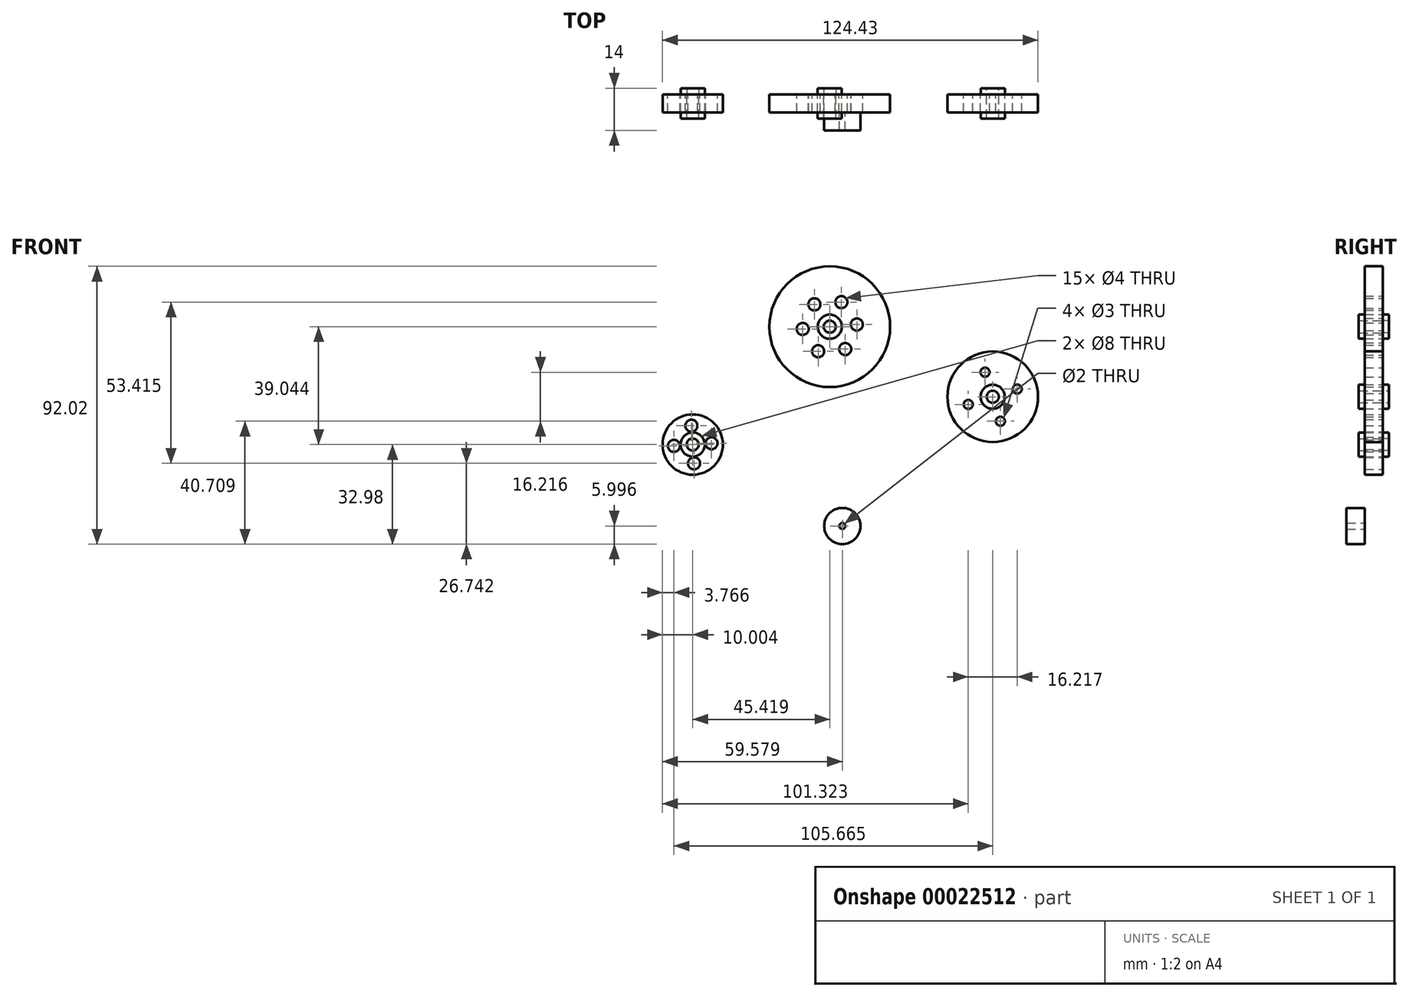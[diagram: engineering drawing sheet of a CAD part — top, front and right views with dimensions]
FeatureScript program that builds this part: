
annotation { "Feature Type Name" : "Feature", "Feature Type Description" : "" }
export const myFeature = defineFeature(function(context is Context, id is Id, definition is map)
    precondition{}
    {
        {
            var Q0;
            Q0=qCreatedBy(makeId("Front.planeOp"),FACE);
            var sketch = newSketch(context, id + "F0", { "sketchPlane" : qUnion([Q0])});
            skCircle(sketch, "E0", {"center": v(-11.19, 16.31) * mm, "radius": 20 * mm});
            skCircle(sketch, "E1", {"center": v(-11.19, 16.31) * mm, "radius": 4 * mm});
            skCircle(sketch, "E2", {"center": v(-11.19, 16.31) * mm, "radius": 2 * mm});
            skCircle(sketch, "E3", {"center": v(-6.07, 8.91) * mm, "radius": 2 * mm});
            skCircle(sketch, "E4.1.0", {"center": v(-2.22, 17.04) * mm, "radius": 2 * mm});
            skCircle(sketch, "E4.2.0", {"center": v(-7.33, 24.45) * mm, "radius": 2 * mm});
            skCircle(sketch, "E4.3.0", {"center": v(-16.3, 23.72) * mm, "radius": 2 * mm});
            skCircle(sketch, "E4.4.0", {"center": v(-20.16, 15.58) * mm, "radius": 2 * mm});
            skCircle(sketch, "E4.5.0", {"center": v(-15.04, 8.18) * mm, "radius": 2 * mm});
            skSolve(sketch);
        }
        {
            var Q0;
            Q0=makeQuery(id+"F0.imprint","IMPRINT",FACE,{"disambiguationData":[TD([[makeQuery(id+"F0.imprint","IMPRINT",EDGE,{"derivedFrom":sQuery(id+"F0.wireOp",EDGE,"E0")}),1.0]])]});
            extrude(context, id + "F1", {"entities" : qUnion([Q0]), "depth" : 6 * mm});
        }
        {
            var Q0;
            Q0=makeQuery(id+"F0.imprint","IMPRINT",FACE,{"disambiguationData":[TD([[makeQuery(id+"F0.imprint","IMPRINT",EDGE,{"derivedFrom":sQuery(id+"F0.wireOp",EDGE,"E1")}),1.0]])]});
            extrude(context, id + "F2", {"entities" : qUnion([Q0]), "operationType" : NewBodyOperationType.ADD, "oppositeDirection" : true, "depth" : 2 * mm});
        }
        {
            var Q0;
            Q0=makeQuery(id+"F0.imprint","IMPRINT",FACE,{"disambiguationData":[TD([[makeQuery(id+"F0.imprint","IMPRINT",EDGE,{"derivedFrom":sQuery(id+"F0.wireOp",EDGE,"E1")}),1.0]])]});
            extrude(context, id + "F3", {"entities" : qUnion([Q0]), "depth" : 8 * mm});
        }
        {
            var Q0;
            Q0=qCreatedBy(makeId("Front.planeOp"),FACE);
            var sketch = newSketch(context, id + "F4", { "sketchPlane" : qUnion([Q0])});
            skCircle(sketch, "E5", {"center": v(42.82, -6.9) * mm, "radius": 15 * mm});
            skCircle(sketch, "E6", {"center": v(42.82, -6.9) * mm, "radius": 4 * mm});
            skCircle(sketch, "E7", {"center": v(42.82, -6.9) * mm, "radius": 2 * mm});
            skCircle(sketch, "E8", {"center": v(45.37, -15) * mm, "radius": 1.5 * mm});
            skCircle(sketch, "E9.1.0", {"center": v(50.93, -4.34) * mm, "radius": 1.5 * mm});
            skCircle(sketch, "E9.2.0", {"center": v(40.27, 1.22) * mm, "radius": 1.5 * mm});
            skCircle(sketch, "E9.3.0", {"center": v(34.71, -9.44) * mm, "radius": 1.5 * mm});
            skSolve(sketch);
        }
        {
            var Q0;
            Q0 = qSketchRegion(id + "F4", true);
            extrude(context, id + "F5", {"entities" : qUnion([Q0]), "depth" : 6 * mm});
        }
        {
            var Q0;
            Q0=makeQuery(id+"F4.imprint","IMPRINT",FACE,{"disambiguationData":[TD([[makeQuery(id+"F4.imprint","IMPRINT",EDGE,{"derivedFrom":sQuery(id+"F4.wireOp",EDGE,"E6")}),1.0]])]});
            extrude(context, id + "F6", {"entities" : qUnion([Q0]), "operationType" : NewBodyOperationType.ADD, "depth" : 8 * mm});
        }
        {
            var Q0;
            Q0=makeQuery(id+"F4.imprint","IMPRINT",FACE,{"disambiguationData":[TD([[makeQuery(id+"F4.imprint","IMPRINT",EDGE,{"derivedFrom":sQuery(id+"F4.wireOp",EDGE,"E6")}),1.0]])]});
            var Q1;
            Q1=sQuery(id+"F4.wireOp",EDGE,"E6");
            extrude(context, id + "F7", {"entities" : qUnion([Q0]), "operationType" : NewBodyOperationType.ADD, "surfaceEntities" : qUnion([Q1]), "oppositeDirection" : true, "depth" : 2 * mm});
        }
        {
            var Q0;
            Q0=qCreatedBy(makeId("Front.planeOp"),FACE);
            var sketch = newSketch(context, id + "F8", { "sketchPlane" : qUnion([Q0])});
            skCircle(sketch, "E10", {"center": v(-56.6, -22.73) * mm, "radius": 10 * mm});
            skCircle(sketch, "E11", {"center": v(-56.6, -22.73) * mm, "radius": 4 * mm});
            skCircle(sketch, "E12", {"center": v(-56.6, -22.73) * mm, "radius": 2 * mm});
            skCircle(sketch, "E13", {"center": v(-56.17, -28.97) * mm, "radius": 2 * mm});
            skCircle(sketch, "E14.1.0", {"center": v(-50.37, -22.3) * mm, "radius": 2 * mm});
            skCircle(sketch, "E14.2.0", {"center": v(-57.04, -16.5) * mm, "radius": 2 * mm});
            skCircle(sketch, "E14.3.0", {"center": v(-62.84, -23.17) * mm, "radius": 2 * mm});
            skSolve(sketch);
        }
        {
            var Q0;
            Q0=makeQuery(id+"F8.imprint","IMPRINT",FACE,{"disambiguationData":[TD([[makeQuery(id+"F8.imprint","IMPRINT",EDGE,{"derivedFrom":sQuery(id+"F8.wireOp",EDGE,"E11")}),-1.0]])]});
            extrude(context, id + "F9", {"entities" : qUnion([Q0]), "depth" : 6 * mm});
        }
        {
            var Q0;
            Q0=makeQuery(id+"F8.imprint","IMPRINT",FACE,{"disambiguationData":[TD([[makeQuery(id+"F8.imprint","IMPRINT",EDGE,{"derivedFrom":sQuery(id+"F8.wireOp",EDGE,"E11")}),1.0]])]});
            extrude(context, id + "F10", {"entities" : qUnion([Q0]), "operationType" : NewBodyOperationType.ADD, "oppositeDirection" : true, "depth" : 2 * mm});
        }
        {
            var Q0;
            Q0=makeQuery(id+"F8.imprint","IMPRINT",FACE,{"disambiguationData":[TD([[makeQuery(id+"F8.imprint","IMPRINT",EDGE,{"derivedFrom":sQuery(id+"F8.wireOp",EDGE,"E11")}),1.0]])]});
            extrude(context, id + "F11", {"entities" : qUnion([Q0]), "depth" : 8 * mm});
        }
        {
            var Q0;
            Q0=makeQuery(id+"F9.opExtrude","CAP_FACE",FACE,{"disambiguationData":[OSD([sQuery(id+"F8.wireOp",EDGE,"E11"),sQuery(id+"F8.wireOp",EDGE,"E13"),sQuery(id+"F8.wireOp",EDGE,"E14.1.0"),sQuery(id+"F8.wireOp",EDGE,"E14.2.0"),sQuery(id+"F8.wireOp",EDGE,"E14.3.0"),sQuery(id+"F8.wireOp",EDGE,"E10")])],"isStart":false});
            var sketch = newSketch(context, id + "F12", { "sketchPlane" : qUnion([Q0])});
            skCircle(sketch, "E15", {"center": v(-7.03, -49.71) * mm, "radius": 6 * mm});
            skCircle(sketch, "E16", {"center": v(-7.03, -49.71) * mm, "radius": 1 * mm});
            skSolve(sketch);
        }
        {
            var Q0;
            Q0=makeQuery(id+"F12.imprint","IMPRINT",FACE,{"disambiguationData":[TD([[makeQuery(id+"F12.imprint","IMPRINT",EDGE,{"derivedFrom":sQuery(id+"F12.wireOp",EDGE,"E15")}),1.0]])]});
            extrude(context, id + "F13", {"entities" : qUnion([Q0]), "depth" : 6 * mm});
        }
    });
